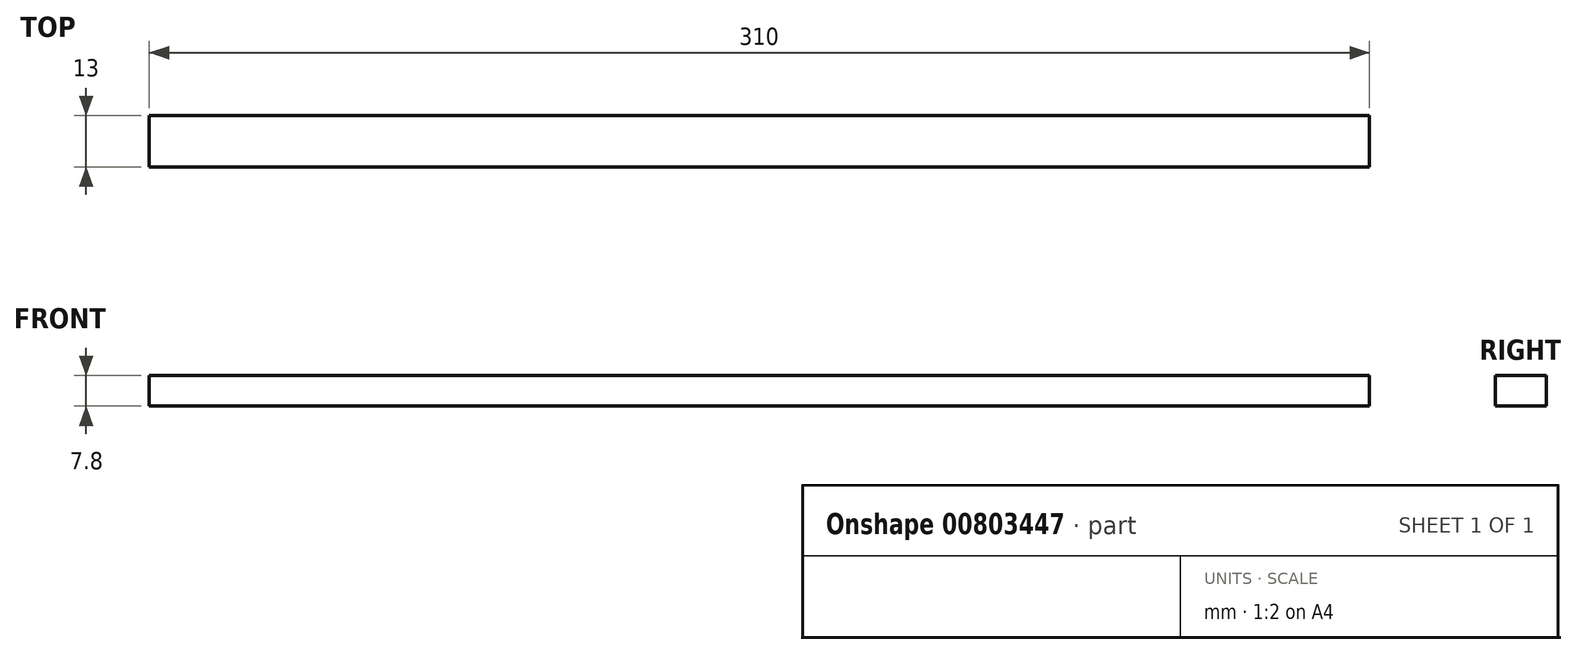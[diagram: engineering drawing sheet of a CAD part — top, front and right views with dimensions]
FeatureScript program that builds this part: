
annotation { "Feature Type Name" : "Feature", "Feature Type Description" : "" }
export const myFeature = defineFeature(function(context is Context, id is Id, definition is map)
    precondition{}
    {
        {
            var Q0;
            Q0=qCreatedBy(makeId("Right.planeOp"),FACE);
            var sketch = newSketch(context, id + "F0", { "sketchPlane" : qUnion([Q0])});
            skLineSegment(sketch, "E0.bottom", {"start": v(6.5, 3.9) * mm, "end": v(-6.5, 3.9) * mm});
            skLineSegment(sketch, "E0.top", {"start": v(6.5, -3.9) * mm, "end": v(-6.5, -3.9) * mm});
            skLineSegment(sketch, "E0.left", {"start": v(6.5, 3.9) * mm, "end": v(6.5, -3.9) * mm});
            skLineSegment(sketch, "E0.right", {"start": v(-6.5, 3.9) * mm, "end": v(-6.5, -3.9) * mm});
            skPoint(sketch, "E0.middle", {"position": v(0, 0) * mm});
            skSolve(sketch);
        }
        {
            var Q0;
            Q0 = qSketchRegion(id + "F0", true);
            extrude(context, id + "F1", {"entities" : qUnion([Q0]), "endBound" : BoundingType.SYMMETRIC, "depth" : 310 * mm, "offsetDistance" : 25 * mm});
        }
    });
